# Revit family: BLAUBERG-KOMFORT_Roto_EC_S280_SE280
name_source: partatom
category: Mechanical Equipment
units: mm (PartAtom-declared; Revit-internal decimal feet)

## family parameters
Always vertical = Yes
Classification = None
Cut with Voids When Loaded = No
OmniClass Number = 23.75.35.14
OmniClass Title = Air Handling Units
Part Type = Normal
Room Calculation Point = No
Round Connector Dimension = Use Diameter
Shared = No
Work Plane-Based = No

## types (2) — shared parameters
B = 520 mm  [stored 1.70604 ft]
B1 = 482 mm  [stored 1.58136 ft]
B2 = 230 mm  [stored 0.754593 ft]
B3 = 136 mm
BackFeetD = 20 mm  [stored 0.0656168 ft]
Casing Material = Painted Steel White
D = 125 mm  [stored 0.410105 ft]
Description = Air Handling Unit
Duct Connection Diameter = 125 mm  [stored 0.410105 ft]
ElBoxA = 65 mm  [stored 0.213255 ft]
ElBoxB = 170 mm  [stored 0.557743 ft]
ElConA = 365 mm  [stored 1.19751 ft]
ElConB = 135 mm  [stored 0.442913 ft]
Extract Air Filter = G4
Family Version = 1.0
FilterCoverH1 = 205 mm  [stored 0.672572 ft]
FilterCoverH2 = 195 mm  [stored 0.639764 ft]
FilterCoverL1 = 76 mm  [stored 0.249344 ft]
FilterCoverL2 = 340 mm  [stored 1.11549 ft]
Front Maintenance Zone Height = 600 mm
Front Maintenance Zone Length = 598 mm  [stored 1.96194 ft]
Front Maintenance Zone Width = 630 mm  [stored 2.06693 ft]
H = 754 mm  [stored 2.47375 ft]
H1 = 630 mm  [stored 2.06693 ft]
H2 = 97 mm  [stored 0.318241 ft]
H3 = 73 mm  [stored 0.239501 ft]
HDuctCon = 50 mm  [stored 0.164042 ft]
Heat Exchanger Material = aluminium
Heat Exchanger Type = rotary
Heat recovery efficiency (%) = 81..90
L = 598 mm  [stored 1.96194 ft]
L1 = 107 mm  [stored 0.35105 ft]
L2 = 243 mm
L3 = 141 mm
L4 = 107 mm  [stored 0.35105 ft]
L5 = 256 mm  [stored 0.839895 ft]
Load Classification = HVAC
Maintenance Zone Material = Maintenance Zone
Manufacturer = Blauberg
Maximum Air Flow = 300 m³/h
Maximum Unit Current Without Electric Heater = 2 A
Maximum Unit Power Without Electric Heater = 195 W
Metal Material = Metal Zinc
Number of Poles = 1
Plastic Material = Polypropylene Black
Power Factor = 1
RPM (min-1) = 2050
SEC Class = A
ServiceDoorB = 20 mm  [stored 0.0656168 ft]
Sound Pressure Level at 3 m (dBA) = 26
Supply Air Filter = F7
Transported Air Temperature (°C) = -25…+40
URL = https://blaubergventilatoren.de
Voltage = 230 V
dBFeets = 68 mm
dLFeets = 45 mm  [stored 0.147638 ft]

## per-type parameters (varying)
| type | Current | Heater power | Maximum Unit Current With Electric Heater | Power | Type Comments | Weight |
| KOMFORT Roto EC S280 S21 | 2 A | 0 W | 2 A | 195 W | Air Handling Unit KOMFORT Roto EC S280 S21 | 63.00 kg |
| KOMFORT Roto EC SE280 S21 | 5 A | 650 W | 5 A | 845 W | Air Handling Unit KOMFORT Roto EC SE280 S21 | 64.00 kg |

note: column(s) folded — value = type name in every type: Model

note: [stored X ft] marks values corroborated as IEEE doubles in the binary element streams (Revit-internal decimal feet)

## geometry (parser evidence)
native form markers: Sweep x9
no freeform markers — native parametric forms only
